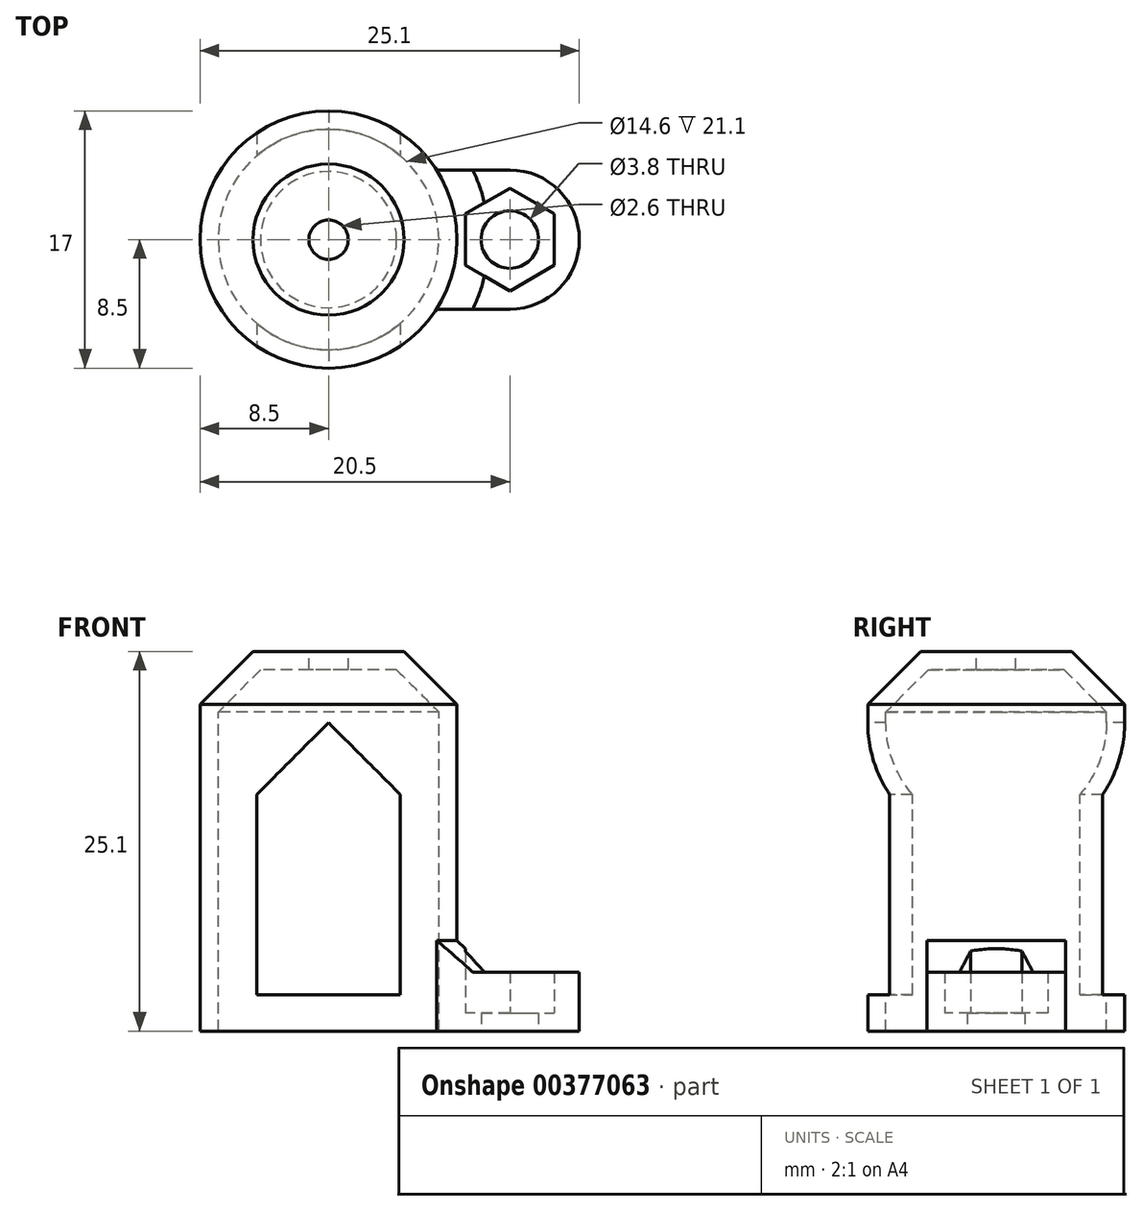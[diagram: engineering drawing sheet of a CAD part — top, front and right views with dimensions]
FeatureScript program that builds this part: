
annotation { "Feature Type Name" : "Feature", "Feature Type Description" : "" }
export const myFeature = defineFeature(function(context is Context, id is Id, definition is map)
    precondition{}
    {
        {
            var Q0;
            Q0=qCreatedBy(makeId("Front.planeOp"),FACE);
            var sketch = newSketch(context, id + "F0", { "sketchPlane" : qUnion([Q0])});
            skLineSegment(sketch, "E0", {"start": v(6.5, 0) * mm, "end": v(6.5, 26.4) * mm});
            skLineSegment(sketch, "E1", {"start": v(4.7, 0) * mm, "end": v(4.7, -6.4) * mm});
            skLineSegment(sketch, "E2", {"start": v(-3.7, 28.3) * mm, "end": v(3.7, 28.3) * mm});
            skPoint(sketch, "E3", {"position": v(0, 28.3) * mm});
            skLineSegment(sketch, "E4", {"start": v(-3.7, 40.8) * mm, "end": v(3.7, 40.8) * mm});
            skLineSegment(sketch, "E5", {"start": v(0, 26.4) * mm, "end": v(0, 0) * mm, "construction": true});
            skSolve(sketch);
        }
        {
            var Q0;
            Q0=qCreatedBy(makeId("Front.planeOp"),FACE);
            var sketch = newSketch(context, id + "F1", { "sketchPlane" : qUnion([Q0])});
            skLineSegment(sketch, "E6", {"start": v(7.3, 16.4) * mm, "end": v(8.5, 16.4) * mm});
            skLineSegment(sketch, "E7", {"start": v(8.5, 16.4) * mm, "end": v(8.5, 38) * mm});
            skLineSegment(sketch, "E8", {"start": v(7.3, 16.4) * mm, "end": v(7.3, 37.5) * mm});
            skLineSegment(sketch, "E9", {"start": v(0, 40.3) * mm, "end": v(4.5, 40.3) * mm});
            skLineSegment(sketch, "E10", {"start": v(4.5, 40.3) * mm, "end": v(7.3, 37.5) * mm});
            skLineSegment(sketch, "E11", {"start": v(0, 41.5) * mm, "end": v(5, 41.5) * mm});
            skLineSegment(sketch, "E12", {"start": v(0, 41.5) * mm, "end": v(0, 40.3) * mm});
            skLineSegment(sketch, "E13", {"start": v(5, 41.5) * mm, "end": v(8.5, 38) * mm});
            skSolve(sketch);
        }
        {
            var Q0;
            Q0 = qSketchRegion(id + "F1", true);
            var Q1;
            Q1=sQuery(id+"F0.wireOp",EDGE,"E5");
            revolve(context, id + "F2", {"entities" : qUnion([Q0]), "axis" : qUnion([Q1]), "revolveType" : RevolveType.FULL});
        }
        {
            var Q0;
            Q0=makeQuery(id+"F2.opRevolve","SWEPT_FACE",FACE,{"disambiguationData":[OSD([sQuery(id+"F1.wireOp",EDGE,"E6")])]});
            var sketch = newSketch(context, id + "F3", { "sketchPlane" : qUnion([Q0])});
            skArc(sketch, "E14", {"start": v(12, -4.6) * mm, "mid": v(16.6, 0) * mm, "end": v(12, 4.6) * mm});
            skLineSegment(sketch, "E15", {"start": v(12, -4.6) * mm, "end": v(7.15, -4.6) * mm});
            skLineSegment(sketch, "E16", {"start": v(12, 4.6) * mm, "end": v(7.15, 4.6) * mm});
            skArc(sketch, "E17", {"start": v(7.15, -4.6) * mm, "mid": v(8.5, 0) * mm, "end": v(7.15, 4.6) * mm});
            skSolve(sketch);
        }
        {
            var Q0;
            Q0 = qSketchRegion(id + "F3", true);
            extrude(context, id + "F4", {"entities" : qUnion([Q0]), "operationType" : NewBodyOperationType.ADD, "oppositeDirection" : true, "depth" : 6 * mm});
        }
        {
            var Q0;
            Q0=makeQuery(id+"F3.imprint","IMPRINT",FACE,{"disambiguationData":[TD([[makeQuery(id+"F3.imprint","IMPRINT",EDGE,{"derivedFrom":sQuery(id+"F3.wireOp",EDGE,"E14")}),1.0]])]});
            cPlane(context, id + "F5", {"entities" : qUnion([Q0]), "cplaneType" : CPlaneType.OFFSET, "offset" : 1.2 * mm, "oppositeDirection" : true, "width" : 150 * mm, "height" : 150 * mm});
        }
        {
            var Q0;
            Q0=qCreatedBy(id+"F5.planeOp",FACE);
            var sketch = newSketch(context, id + "F6", { "sketchPlane" : qUnion([Q0])});
            skCircle(sketch, "E18.cCircle", {"center": v(12, 0) * mm, "radius": 2.95 * mm, "construction": true});
            skLineSegment(sketch, "E18.0", {"start": v(14.95, -1.7) * mm, "end": v(14.95, 1.7) * mm});
            skLineSegment(sketch, "E18.1", {"start": v(12, -3.4) * mm, "end": v(14.95, -1.7) * mm});
            skLineSegment(sketch, "E18.2", {"start": v(9.05, -1.7) * mm, "end": v(12, -3.4) * mm});
            skLineSegment(sketch, "E18.3", {"start": v(9.05, 1.7) * mm, "end": v(9.05, -1.7) * mm});
            skLineSegment(sketch, "E18.4", {"start": v(12, 3.4) * mm, "end": v(9.05, 1.7) * mm});
            skLineSegment(sketch, "E18.5", {"start": v(14.95, 1.7) * mm, "end": v(12, 3.4) * mm});
            skPoint(sketch, "E18.0.midPoint", {"position": v(14.95, 0) * mm});
            skSolve(sketch);
        }
        {
            var Q0;
            Q0=qCreatedBy(makeId("Front.planeOp"),FACE);
            var sketch = newSketch(context, id + "F7", { "sketchPlane" : qUnion([Q0])});
            skLineSegment(sketch, "E19", {"start": v(8.5, 16.4) * mm, "end": v(8.5, 22.4) * mm, "construction": true});
            skLineSegment(sketch, "E20", {"start": v(10.6, 20.3) * mm, "end": v(16.6, 20.3) * mm});
            skLineSegment(sketch, "E21", {"start": v(8.5, 22.4) * mm, "end": v(10.6, 20.3) * mm});
            skLineSegment(sketch, "E22", {"start": v(16.6, 20.3) * mm, "end": v(16.6, 22.4) * mm});
            skLineSegment(sketch, "E23", {"start": v(16.6, 22.4) * mm, "end": v(8.5, 22.4) * mm});
            skSolve(sketch);
        }
        {
            var Q0;
            Q0 = qSketchRegion(id + "F7", true);
            var Q1;
            Q1=sQuery(id+"F0.wireOp",EDGE,"E5");
            revolve(context, id + "F8", {"operationType" : NewBodyOperationType.REMOVE, "entities" : qUnion([Q0]), "axis" : qUnion([Q1]), "revolveType" : RevolveType.FULL, "oppositeDirection" : true});
        }
        {
            var Q0;
            Q0 = qSketchRegion(id + "F6", true);
            extrude(context, id + "F9", {"entities" : qUnion([Q0]), "operationType" : NewBodyOperationType.REMOVE, "endBound" : BoundingType.UP_TO_NEXT, "oppositeDirection" : true, "depth" : 25 * mm});
        }
        {
            var Q0;
            Q0=makeQuery(id+"F3.imprint","IMPRINT",FACE,{"disambiguationData":[TD([[makeQuery(id+"F3.imprint","IMPRINT",EDGE,{"derivedFrom":sQuery(id+"F3.wireOp",EDGE,"E14")}),1.0]])]});
            var sketch = newSketch(context, id + "F10", { "sketchPlane" : qUnion([Q0])});
            skCircle(sketch, "E24", {"center": v(12, 0) * mm, "radius": 1.9 * mm});
            skSolve(sketch);
        }
        {
            var Q0;
            Q0 = qSketchRegion(id + "F10", true);
            extrude(context, id + "F11", {"entities" : qUnion([Q0]), "operationType" : NewBodyOperationType.REMOVE, "endBound" : BoundingType.UP_TO_NEXT, "oppositeDirection" : true, "depth" : 25 * mm});
        }
        {
            var Q0;
            Q0=qCreatedBy(makeId("Front.planeOp"),FACE);
            var sketch = newSketch(context, id + "F12", { "sketchPlane" : qUnion([Q0])});
            skLineSegment(sketch, "E25.bottom", {"start": v(-4.75, 18.8) * mm, "end": v(4.75, 18.8) * mm});
            skLineSegment(sketch, "E25.left", {"start": v(-4.75, 18.8) * mm, "end": v(-4.75, 32.05) * mm});
            skLineSegment(sketch, "E25.right", {"start": v(4.75, 18.8) * mm, "end": v(4.75, 32.05) * mm});
            skPoint(sketch, "E26", {"position": v(0, 18.8) * mm});
            skLineSegment(sketch, "E27", {"start": v(-4.75, 32.05) * mm, "end": v(0, 36.8) * mm});
            skLineSegment(sketch, "E28", {"start": v(0, 36.8) * mm, "end": v(4.75, 32.05) * mm});
            skPoint(sketch, "E29.visualSharp", {"position": v(-4.75, 32.05) * mm});
            skPoint(sketch, "E30.visualSharp", {"position": v(4.75, 32.05) * mm});
            skPoint(sketch, "E31.visualSharp", {"position": v(-4.75, 18.8) * mm});
            skPoint(sketch, "E32.visualSharp", {"position": v(4.75, 18.8) * mm});
            skPoint(sketch, "E33.visualSharp", {"position": v(0, 36.8) * mm});
            skSolve(sketch);
        }
        {
            var Q0;
            Q0 = qSketchRegion(id + "F12", true);
            extrude(context, id + "F13", {"entities" : qUnion([Q0]), "operationType" : NewBodyOperationType.REMOVE, "endBound" : BoundingType.THROUGH_ALL, "oppositeDirection" : true, "depth" : 25 * mm, "hasSecondDirection" : true, "secondDirectionBound" : SecondDirectionBoundingType.THROUGH_ALL, "secondDirectionOppositeDirection" : false, "secondDirectionDepth" : 25 * mm});
        }
        {
            var Q0;
            Q0=qCreatedBy(makeId("Right.planeOp"),FACE);
            var sketch = newSketch(context, id + "F14", { "sketchPlane" : qUnion([Q0])});
            skLineSegment(sketch, "E34.bottom", {"start": v(-4.75, 22.4) * mm, "end": v(4.75, 22.4) * mm});
            skLineSegment(sketch, "E34.top", {"start": v(-4.75, 32.05) * mm, "end": v(4.75, 32.05) * mm, "construction": true});
            skLineSegment(sketch, "E34.left", {"start": v(-4.75, 22.4) * mm, "end": v(-4.75, 32.05) * mm});
            skLineSegment(sketch, "E34.right", {"start": v(4.75, 22.4) * mm, "end": v(4.75, 32.05) * mm});
            skPoint(sketch, "E35", {"position": v(0, 22.4) * mm});
            skLineSegment(sketch, "E36", {"start": v(-4.75, 32.05) * mm, "end": v(0, 36.8) * mm});
            skLineSegment(sketch, "E37", {"start": v(0, 36.8) * mm, "end": v(4.75, 32.05) * mm});
            skPoint(sketch, "E38.visualSharp", {"position": v(-4.75, 32.05) * mm});
            skPoint(sketch, "E39.visualSharp", {"position": v(4.75, 32.05) * mm});
            skPoint(sketch, "E40.visualSharp", {"position": v(-4.75, 22.4) * mm});
            skPoint(sketch, "E41.visualSharp", {"position": v(4.75, 22.4) * mm});
            skPoint(sketch, "E42.visualSharp", {"position": v(0, 36.8) * mm});
            skSolve(sketch);
        }
        {
            var Q0;
            Q0=makeQuery(id+"F2.opRevolve","SWEPT_FACE",FACE,{"disambiguationData":[OSD([sQuery(id+"F1.wireOp",EDGE,"E11")])]});
            var sketch = newSketch(context, id + "F15", { "sketchPlane" : qUnion([Q0])});
            skCircle(sketch, "E43", {"center": v(0, 0) * mm, "radius": 1.3 * mm});
            skSolve(sketch);
        }
        {
            var Q0;
            Q0 = qSketchRegion(id + "F15", true);
            extrude(context, id + "F16", {"entities" : qUnion([Q0]), "operationType" : NewBodyOperationType.REMOVE, "endBound" : BoundingType.UP_TO_NEXT, "oppositeDirection" : true, "depth" : 25 * mm});
        }
    });
